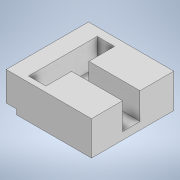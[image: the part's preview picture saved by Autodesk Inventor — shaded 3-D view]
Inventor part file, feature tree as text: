
AUTODESK INVENTOR PART (.ipt)
format: ipt  version: 2022.3 (Build 263350000, 350)  size: 369,152 bytes
history: native  units: mm
features: extrude x8, sketch x6, thicken_offset x3, hole x1, projected_geometry x1
ambient origin geometry x8: Origin, YZ Plane, XZ Plane, XY Plane, X Axis, Y Axis, Z Axis, Center Point
bodies: Solid1 (feature_tree)
feature tree (19):
  sketch  "Sketch1"  dims[d1=200.0mm d2=35.0mm]
  extrude  "Extrusion1"  Depth=35.0mm
  extrude  "Extrusion2"  Depth=5.0mm
  extrude  "Extrusion3"  Depth=30.0mm
  extrude  "Extrusion4"  Depth=10.0mm TaperAngle=0.0deg
  sketch  "Sketch3"  dims[d5=20.0mm d6=30.0mm d8=40.0mm d9=30.0mm d11=40.0mm]
  extrude  "Extrusion6"  Depth=22.0mm
  extrude  "Extrusion7"  Depth=1.5mm TaperAngle=0.0deg
  hole  "Hole1"  [1 undecoded]
  extrude  "Extrusion8"  TaperAngle=120.0deg  [1 undecoded]
  thicken_offset  "Thicken1"
  thicken_offset  "Thicken2"
  extrude  "Extrusion9"  Depth=10.0mm
  thicken_offset  "Thicken3"
  sketch  "Sketch2"  dims[d3=5.0mm d4=5.0mm]
  projected_geometry  "Projected Loop1"
  sketch  "Sketch4"  dims[d14=10.0mm d15=0.0mm d16=10.0mm d17=0.0mm]
  sketch  "Sketch5"  dims[d18=2.5mm d19=0.0mm d20=22.0mm]
  sketch  "Sketch6"  dims[d21=3.0mm d22=1.5mm d23=0.0mm d24=15.0mm d25=120.0deg d26=10.0mm d27=5.0mm d28=20.0mm d29=90.0deg d30=5.0mm d31=2.5mm d32=5.0mm d33=20.0mm d35=120.0deg d37=30.0mm d39=40.0mm d40=30.0mm d42=40.0mm d45=30.0mm d47=40.0mm d48=30.0mm d50=40.0mm d55=10.0mm d56=0.0mm d57=10.0mm d58=0.0mm d59=40.0mm d60=2.2mm d61=6.0mm d62=3.1mm d63=4.1mm d64=90.0deg d65=2.2mm d66=0.0mm d67=10.0mm d68=0.0mm d69=0.05mm d70=0.1mm d71=0.2mm d72=0.2mm d73=10.0mm d74=0.0mm d75=0.3mm d76=0.2mm d77=0.75mm d78=0.375mm]
note: 2 required parameter values undecoded (feature->parameter linkage not recoverable at this tier; creation-order binding heuristic only, values carry confidence <= 0.55)
